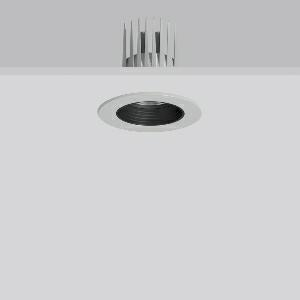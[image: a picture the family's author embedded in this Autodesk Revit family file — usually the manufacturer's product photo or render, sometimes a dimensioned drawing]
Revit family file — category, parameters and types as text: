
# Revit family: heledon_mini_e_901746_004_1_d955
name_source: partatom
category: Lighting Fixtures
units: mm (PartAtom-declared; Revit-internal decimal feet)

## family parameters
Cut with Voids When Loaded = No
Host = Face
Light Source = No
Part Type = Normal
Room Calculation Point = No
Round Connector Dimension = Use Diameter
Shared = No

## types (1)
- HELEDON mini E (1 x LED Modul 940, 2450 lm, 4000)
    Apparent Load = 20 VA
    Approval mark = CE
    CIE Flux Codes = 80 99 100 100 100
    Color Rendering = 92
    Color Temperature = 4000
    Default Elevation = 1800 mm
    Description = Series: HELEDON mini
Round recessed downlight. Housing: die-cast aluminium, powder-coated. Black plastic ring and recessed LED to prevent glare from the side. Optical assembly with lens made of plastic (polycarbonate) for the best homogeneous light distribution - can be changed without tools. Best colour rendering index Ra>90. Suitable for Recessed ceiling mounting. Installation without tools thanks to spring fastening system. Including separate LED converter with connecting cable 600 mm.High quality converter without flickering and stroboscopic effect. Through-wiring box (5 pole) available as accessory. The following accessories can be mounted without use of tools: interchangeable lenses, decorative glasses, honeycomb louvre, clear and frosted diffusers, white interchangeable plastic ring. 
Colour: silver
Diameter: 124 mm
Height: 3 mm
Cut-out diameter: 114 mm
Recess height: 170 mm
Luminaire: recess height: 120 mm
Lamp: LED
Socket: without socket
Colour temperature: 4000K
Colour rendering index (CRI): 92
System power: 20 W
Rated luminous flux: 2450 lm
Luminous efficiency: 123 lm/W
Control gear: Regulated power supply
Protection class: II
Type of protection: IP 20
    Height = 0 mm  [stored 0 ft]
    Lamp = 1 x LED Modul 940
    Lamp Light Flux = 2450 lm
    Lamp count = 1
    Length = 124 mm  [stored 0.406824 ft]
    Lifetime = 50000 h
    Luminous efficacy = 123 lm/W
    Manufacturer = RZB
    ModVariant = No
    Model = 901746.004.1
    Mounting Place = Ceiling
    Mounting Type = Recessed
    Number of Poles = 1
    OnlyDefault = Yes
    Power Factor = 1
    Product Name = HELEDON mini E
    Product group = Recessed downlights
    ProductGroupID = 402
    Protection Class = Protection class II
    Protection Degree = IP 20
    RLX_Detail_Level = 1
    RLX_Emergency_Light_Flux = 0 lm
    RLX_Emergency_Type = 0
    RLX_Emergency_Type_DB = No
    RlxData = <blob elided: 127757 chars, md5=b027fbcf>
    Socket = socket
    Standby Power = 0 W
    System Light Flux = 2450 lm
    System Power = 20 W
    Type Comments = Product without accessories
    Type Image = 901656.004.jpg
    URL = http://relux.com
    VarID = ---
    Voltage = 230 V
    Voltage Range = 220-240 V
    Weight = 0.00 kg
    Width = 0 mm  [stored 0 ft]

note: [stored X ft] marks values corroborated as IEEE doubles in the binary element streams (Revit-internal decimal feet)

## geometry (parser evidence)
native form markers: Blend x4, Sweep x10
no freeform markers — native parametric forms only
